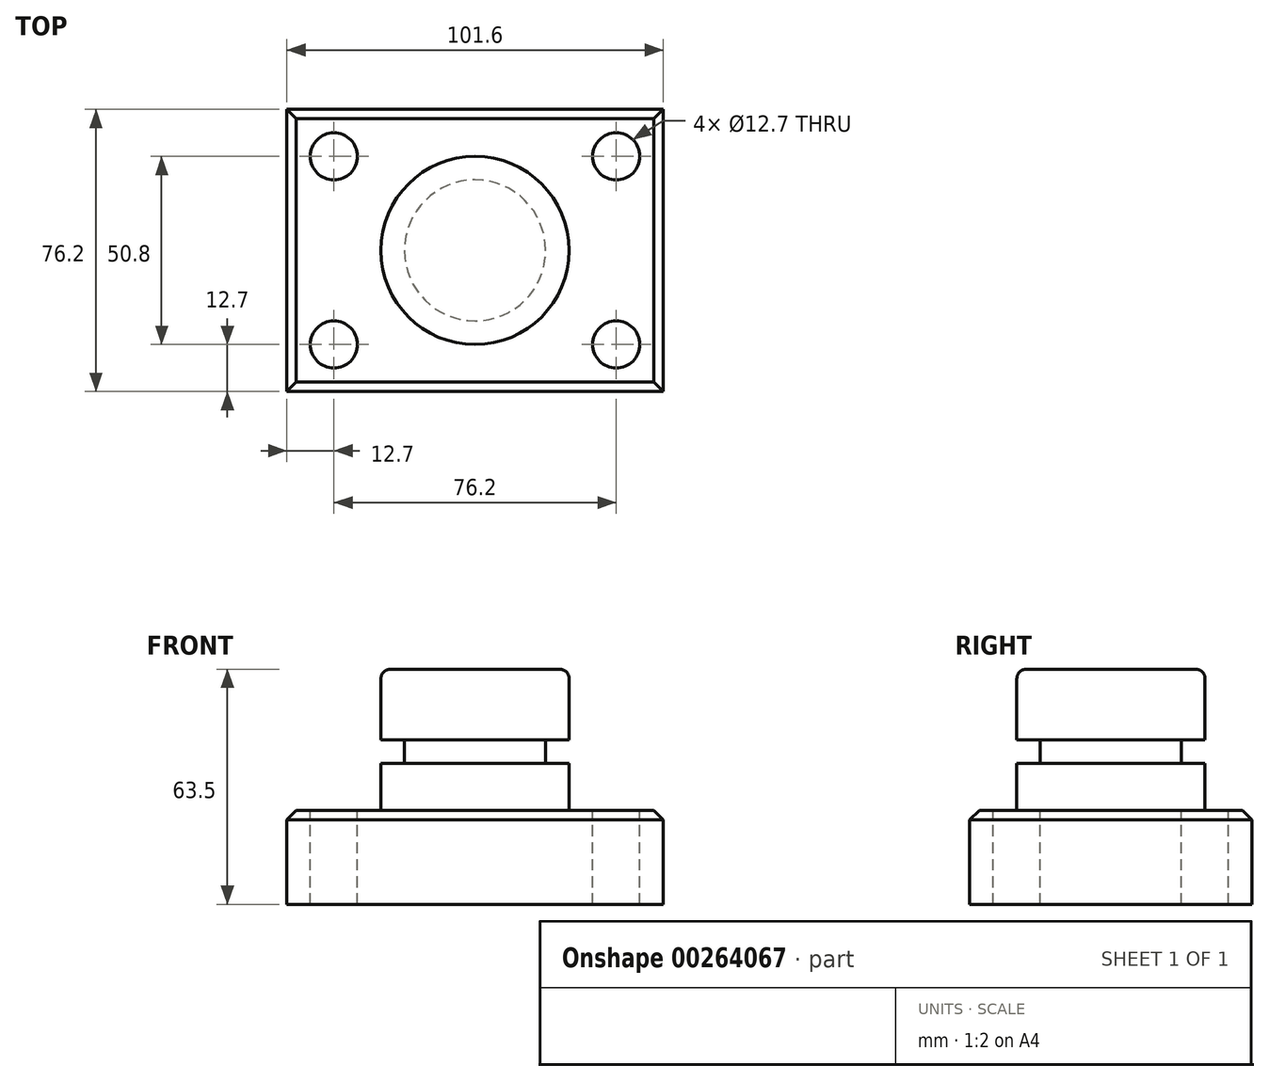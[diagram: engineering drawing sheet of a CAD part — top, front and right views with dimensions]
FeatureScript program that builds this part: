
annotation { "Feature Type Name" : "Feature", "Feature Type Description" : "" }
export const myFeature = defineFeature(function(context is Context, id is Id, definition is map)
    precondition{}
    {
        {
            var Q0;
            Q0=qCreatedBy(makeId("Top.planeOp"),FACE);
            var sketch = newSketch(context, id + "F0", { "sketchPlane" : qUnion([Q0])});
            skLineSegment(sketch, "E0.bottom", {"start": v(-50.8, 38.1) * mm, "end": v(50.8, 38.1) * mm});
            skLineSegment(sketch, "E0.top", {"start": v(-50.8, -38.1) * mm, "end": v(50.8, -38.1) * mm});
            skLineSegment(sketch, "E0.left", {"start": v(-50.8, 38.1) * mm, "end": v(-50.8, -38.1) * mm});
            skLineSegment(sketch, "E0.right", {"start": v(50.8, 38.1) * mm, "end": v(50.8, -38.1) * mm});
            skPoint(sketch, "E0.middle", {"position": v(0, 0) * mm});
            skSolve(sketch);
        }
        {
            var Q0;
            Q0 = qSketchRegion(id + "F0", true);
            extrude(context, id + "F1", {"entities" : qUnion([Q0]), "depth" : 25.4 * mm});
        }
        {
            var Q0;
            Q0=makeQuery(id+"F1.opExtrude","CAP_FACE",FACE,{"disambiguationData":[OSD([sQuery(id+"F0.wireOp",EDGE,"E0.bottom"),sQuery(id+"F0.wireOp",EDGE,"E0.top"),sQuery(id+"F0.wireOp",EDGE,"E0.left"),sQuery(id+"F0.wireOp",EDGE,"E0.right")])],"isStart":false});
            var sketch = newSketch(context, id + "F2", { "sketchPlane" : qUnion([Q0])});
            skCircle(sketch, "E1", {"center": v(-38.1, 25.4) * mm, "radius": 6.35 * mm});
            skCircle(sketch, "E2", {"center": v(38.1, 25.4) * mm, "radius": 6.35 * mm});
            skCircle(sketch, "E3", {"center": v(38.1, -25.4) * mm, "radius": 6.35 * mm});
            skCircle(sketch, "E4", {"center": v(-38.1, -25.4) * mm, "radius": 6.35 * mm});
            skSolve(sketch);
        }
        {
            var Q0;
            Q0 = qSketchRegion(id + "F2", true);
            extrude(context, id + "F3", {"entities" : qUnion([Q0]), "operationType" : NewBodyOperationType.REMOVE, "oppositeDirection" : true, "depth" : 25.4 * mm});
        }
        {
            var Q0;
            Q0=qCreatedBy(makeId("Front.planeOp"),FACE);
            var sketch = newSketch(context, id + "F4", { "sketchPlane" : qUnion([Q0])});
            skLineSegment(sketch, "E5.bottom", {"start": v(-25.4, 63.5) * mm, "end": v(0, 63.5) * mm});
            skLineSegment(sketch, "E5.top", {"start": v(-25.4, 25.4) * mm, "end": v(0, 25.4) * mm});
            skLineSegment(sketch, "E5.left", {"start": v(-25.4, 63.5) * mm, "end": v(-25.4, 25.4) * mm});
            skLineSegment(sketch, "E5.right", {"start": v(0, 63.5) * mm, "end": v(0, 25.4) * mm});
            skSolve(sketch);
        }
        {
            var Q0;
            Q0=makeQuery(id+"F4.imprint","IMPRINT",FACE,{"disambiguationData":[TD([[makeQuery(id+"F4.imprint","IMPRINT",EDGE,{"derivedFrom":sQuery(id+"F4.wireOp",EDGE,"E5.bottom")}),-1.0]])]});
            var Q1;
            Q1=sQuery(id+"F4.wireOp",EDGE,"E5.right");
            revolve(context, id + "F5", {"operationType" : NewBodyOperationType.ADD, "entities" : qUnion([Q0]), "axis" : qUnion([Q1]), "revolveType" : RevolveType.FULL});
        }
        {
            var Q0;
            Q0=qCreatedBy(makeId("Front.planeOp"),FACE);
            var sketch = newSketch(context, id + "F6", { "sketchPlane" : qUnion([Q0])});
            skLineSegment(sketch, "E6.bottom", {"start": v(-42.06, 44.45) * mm, "end": v(-19.05, 44.45) * mm});
            skLineSegment(sketch, "E6.top", {"start": v(-42.06, 38.1) * mm, "end": v(-19.05, 38.1) * mm});
            skLineSegment(sketch, "E6.left", {"start": v(-42.06, 44.45) * mm, "end": v(-42.06, 38.1) * mm});
            skLineSegment(sketch, "E6.right", {"start": v(-19.05, 44.45) * mm, "end": v(-19.05, 38.1) * mm});
            skSolve(sketch);
        }
        {
            var Q0;
            Q0=makeQuery(id+"F6.imprint","IMPRINT",FACE,{"disambiguationData":[TD([[makeQuery(id+"F6.imprint","IMPRINT",EDGE,{"derivedFrom":sQuery(id+"F6.wireOp",EDGE,"E6.bottom")}),-1.0]])]});
            var Q1;
            Q1=makeQuery(id+"F5.opRevolve","SWEPT_FACE",FACE,{"disambiguationData":[OSD([sQuery(id+"F4.wireOp",EDGE,"E5.left")])]});
            revolve(context, id + "F7", {"operationType" : NewBodyOperationType.REMOVE, "entities" : qUnion([Q0]), "axis" : qUnion([Q1]), "revolveType" : RevolveType.FULL, "oppositeDirection" : true});
        }
        {
            var Q0;
            {var subQ0=sQuery(id+"F0.wireOp",EDGE,"E0.left");var subQ1=sQuery(id+"F0.wireOp",EDGE,"E0.top");Q0=makeQuery(id+"F5.boolean.opBoolean","SPLIT",EDGE,{"disambiguationData":[TD([makeQuery(id+"F1.opExtrude","SWEPT_FACE",FACE,{"disambiguationData":[OSD([subQ0])]})])],"derivedFrom":makeQuery(id+"F1.opExtrude","CAP_EDGE",EDGE,{"disambiguationData":[OSD([subQ1])],"isStart":false})});}
            var Q1;
            Q1=makeQuery(id+"F1.opExtrude","CAP_EDGE",EDGE,{"disambiguationData":[OSD([sQuery(id+"F0.wireOp",EDGE,"E0.right")])],"isStart":false});
            var Q2;
            Q2=makeQuery(id+"F1.opExtrude","CAP_EDGE",EDGE,{"disambiguationData":[OSD([sQuery(id+"F0.wireOp",EDGE,"E0.left")])],"isStart":false});
            var Q3;
            {var subQ0=sQuery(id+"F0.wireOp",EDGE,"E0.bottom");var subQ1=sQuery(id+"F0.wireOp",EDGE,"E0.left");Q3=makeQuery(id+"F5.boolean.opBoolean","SPLIT",EDGE,{"disambiguationData":[TD([makeQuery(id+"F1.opExtrude","SWEPT_FACE",FACE,{"disambiguationData":[OSD([subQ1])]})])],"derivedFrom":makeQuery(id+"F1.opExtrude","CAP_EDGE",EDGE,{"disambiguationData":[OSD([subQ0])],"isStart":false})});}
            chamfer(context, id + "F8", {"entities" : qUnion([Q0, Q1, Q2, Q3]), "width" : 2.54 * mm, "tangentPropagation" : true});
        }
        {
            var Q0;
            Q0=makeQuery(id+"F5.opRevolve","SWEPT_EDGE",EDGE,{"disambiguationData":[OSD([sQuery(id+"F4.wireOp",EDGE,"E5.bottom"),sQuery(id+"F4.wireOp",EDGE,"E5.left")])]});
            var Q1;
            Q1=makeQuery(id+"F5.opRevolve","SWEPT_EDGE",EDGE,{"disambiguationData":[OSD([sQuery(id+"F4.wireOp",EDGE,"E5.top"),sQuery(id+"F4.wireOp",EDGE,"E5.left")])]});
            fillet(context, id + "F9", {"entities" : qUnion([Q0, Q1]), "radius" : 2.54 * mm, "tangentPropagation" : true, "allowEdgeOverflow" : false});
        }
    });
